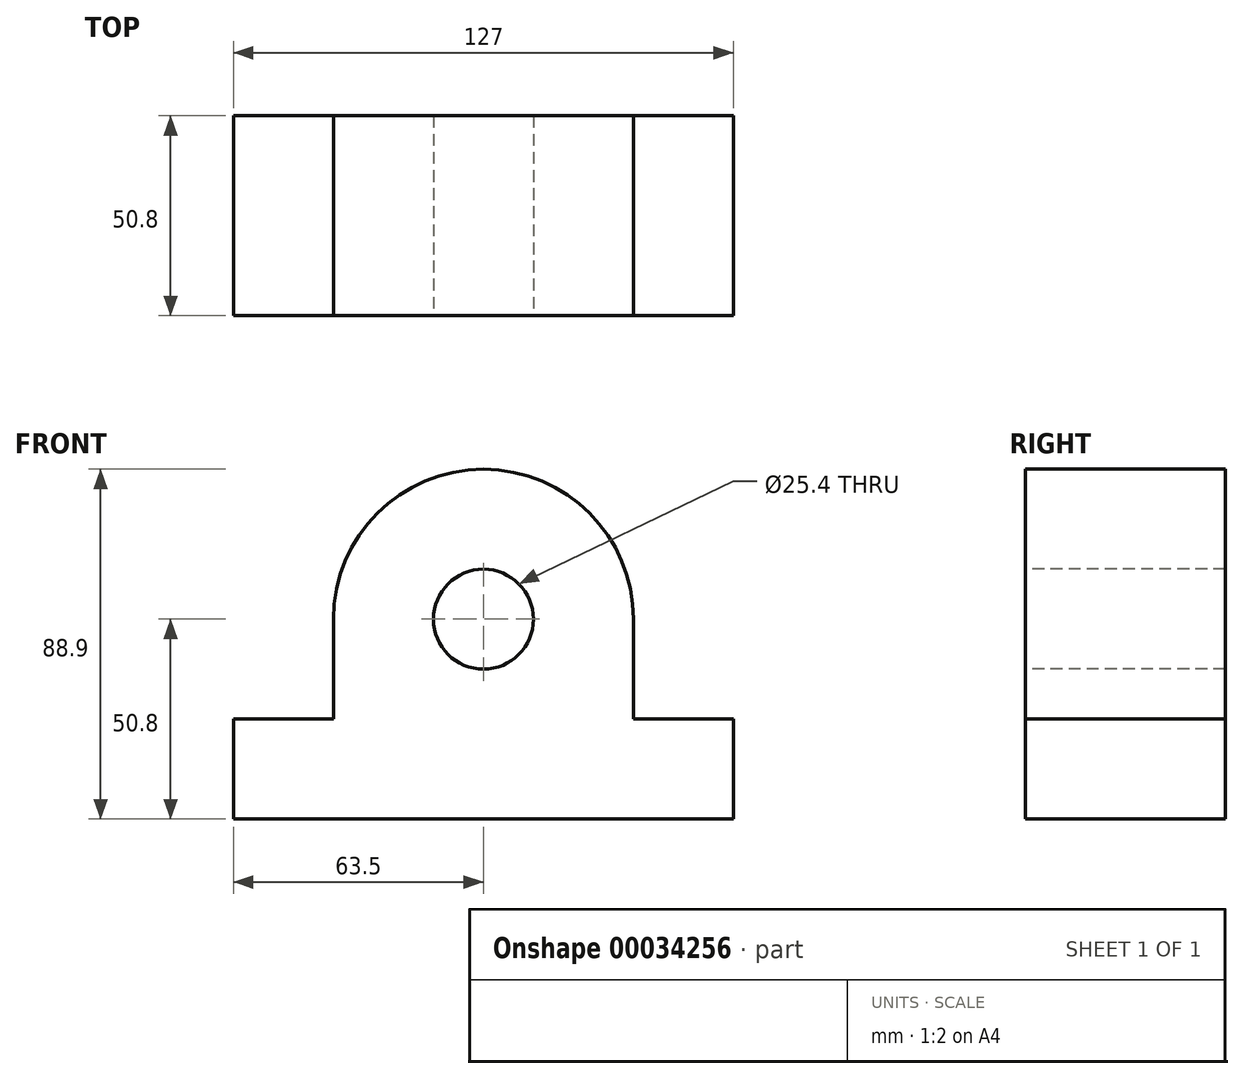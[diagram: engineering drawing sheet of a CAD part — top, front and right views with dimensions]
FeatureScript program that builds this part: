
annotation { "Feature Type Name" : "Feature", "Feature Type Description" : "" }
export const myFeature = defineFeature(function(context is Context, id is Id, definition is map)
    precondition{}
    {
        {
            var Q0;
            Q0=qCreatedBy(makeId("Front.planeOp"),FACE);
            var sketch = newSketch(context, id + "F0", { "sketchPlane" : qUnion([Q0])});
            skLineSegment(sketch, "E0.bottom", {"start": v(0, 0) * mm, "end": v(-25.4, 0) * mm});
            skLineSegment(sketch, "E0.top", {"start": v(0, -25.4) * mm, "end": v(-127, -25.4) * mm});
            skLineSegment(sketch, "E0.left", {"start": v(0, 0) * mm, "end": v(0, -25.4) * mm});
            skLineSegment(sketch, "E0.right", {"start": v(-127, 0) * mm, "end": v(-127, -25.4) * mm});
            skLineSegment(sketch, "E1.left", {"start": v(-25.4, 0) * mm, "end": v(-25.4, 25.4) * mm});
            skLineSegment(sketch, "E1.right", {"start": v(-101.6, 0) * mm, "end": v(-101.6, 25.4) * mm});
            skArc(sketch, "E2.trimOffspring", {"start": v(-25.4, 25.4) * mm, "mid": v(-63.5, 63.5) * mm, "end": v(-101.6, 25.4) * mm});
            skLineSegment(sketch, "E3.trimOffspring", {"start": v(-101.6, 0) * mm, "end": v(-127, 0) * mm});
            skSolve(sketch);
        }
        {
            var Q0;
            Q0=makeQuery(id+"F0.imprint","IMPRINT",FACE,{"disambiguationData":[TD([[makeQuery(id+"F0.imprint","IMPRINT",EDGE,{"derivedFrom":sQuery(id+"F0.wireOp",EDGE,"E0.bottom")}),1.0]])]});
            extrude(context, id + "F1", {"entities" : qUnion([Q0]), "depth" : 50.8 * mm});
        }
        {
            var Q0;
            Q0=makeQuery(id+"F1.opExtrude","CAP_FACE",FACE,{"disambiguationData":[OSD([sQuery(id+"F0.wireOp",EDGE,"E0.bottom"),sQuery(id+"F0.wireOp",EDGE,"E0.top"),sQuery(id+"F0.wireOp",EDGE,"E0.left"),sQuery(id+"F0.wireOp",EDGE,"E0.right"),sQuery(id+"F0.wireOp",EDGE,"E1.left"),sQuery(id+"F0.wireOp",EDGE,"E1.right"),sQuery(id+"F0.wireOp",EDGE,"E2.trimOffspring"),sQuery(id+"F0.wireOp",EDGE,"E3.trimOffspring")])],"isStart":false});
            var sketch = newSketch(context, id + "F2", { "sketchPlane" : qUnion([Q0])});
            skCircle(sketch, "E4", {"center": v(-63.5, 25.4) * mm, "radius": 12.7 * mm});
            skSolve(sketch);
        }
        {
            var Q0;
            Q0=makeQuery(id+"F2.imprint","IMPRINT",FACE,{"disambiguationData":[TD([[makeQuery(id+"F2.imprint","IMPRINT",EDGE,{"derivedFrom":sQuery(id+"F2.wireOp",EDGE,"E4")}),1.0]])]});
            extrude(context, id + "F3", {"entities" : qUnion([Q0]), "operationType" : NewBodyOperationType.REMOVE, "endBound" : BoundingType.THROUGH_ALL, "oppositeDirection" : true, "depth" : 25.4 * mm});
        }
    });
